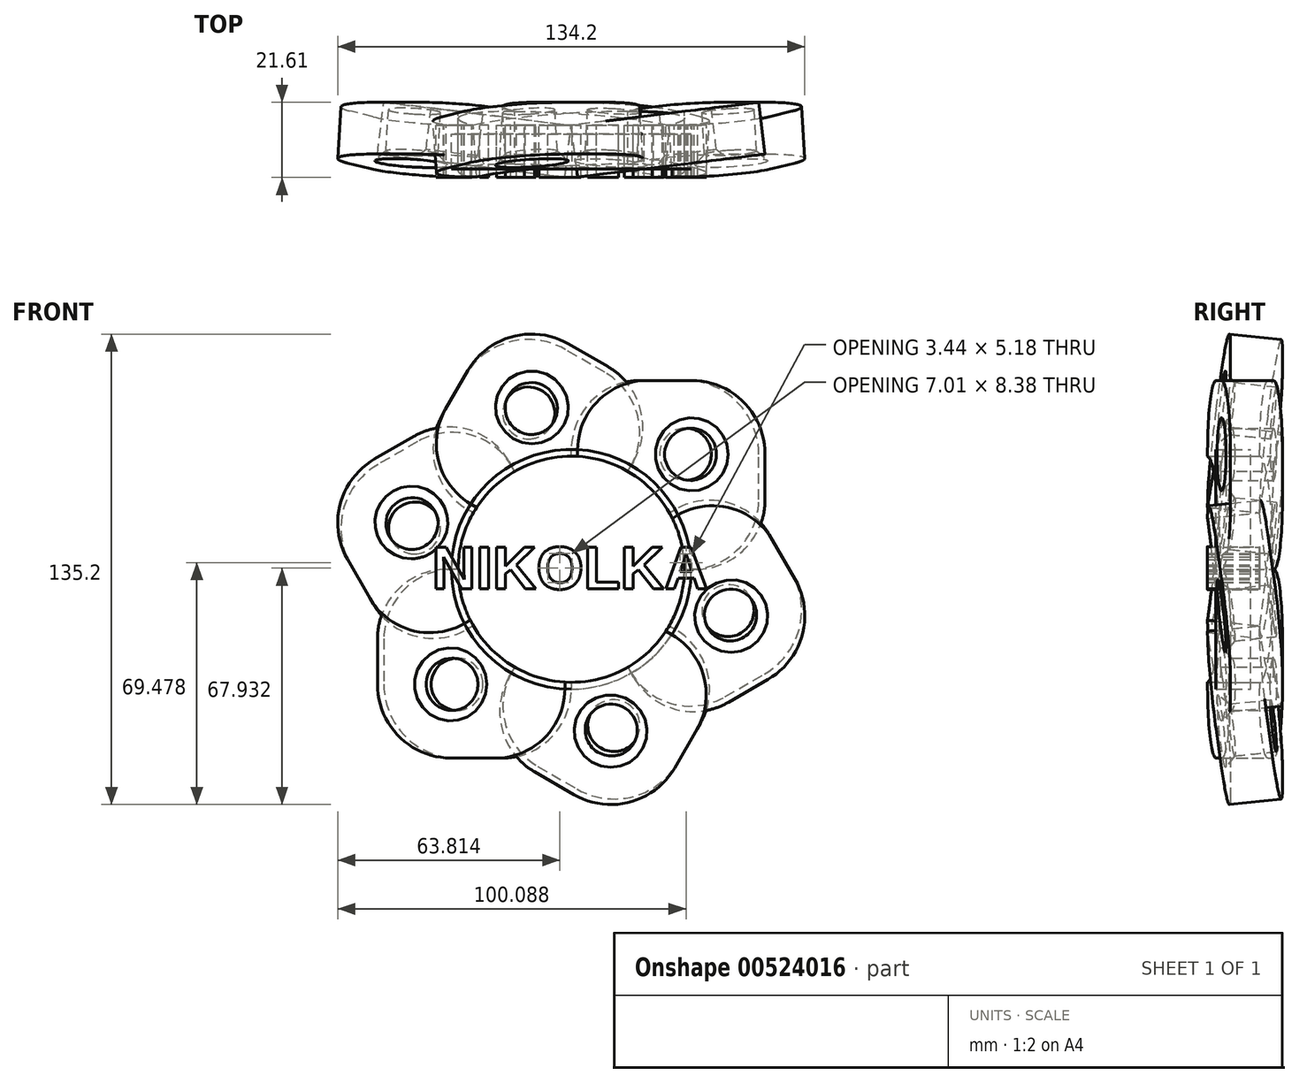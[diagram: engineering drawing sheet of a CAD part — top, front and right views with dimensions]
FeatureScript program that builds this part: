
annotation { "Feature Type Name" : "Feature", "Feature Type Description" : "" }
export const myFeature = defineFeature(function(context is Context, id is Id, definition is map)
    precondition{}
    {
        {
            var Q0;
            Q0=qCreatedBy(makeId("Front.planeOp"),FACE);
            var sketch = newSketch(context, id + "F0", { "sketchPlane" : qUnion([Q0])});
            skLineSegment(sketch, "E0.bottom", {"start": v(0, 0) * mm, "end": v(34.25, 0) * mm});
            skLineSegment(sketch, "E0.top", {"start": v(20, 54.25) * mm, "end": v(33.05, 54.25) * mm});
            skLineSegment(sketch, "E0.left", {"start": v(0, 0) * mm, "end": v(0, 34.25) * mm});
            skLineSegment(sketch, "E0.right", {"start": v(54.25, 20) * mm, "end": v(54.25, 33.05) * mm});
            skPoint(sketch, "E1.visualSharp", {"position": v(54.25, 54.25) * mm});
            skArc(sketch, "E1.filletArc", {"start": v(54.25, 33.05) * mm, "mid": v(48.04, 48.04) * mm, "end": v(33.05, 54.25) * mm});
            skPoint(sketch, "E2.visualSharp", {"position": v(0, 54.25) * mm});
            skArc(sketch, "E2.filletArc", {"start": v(20, 54.25) * mm, "mid": v(5.86, 48.4) * mm, "end": v(0, 34.25) * mm});
            skPoint(sketch, "E3.visualSharp", {"position": v(54.25, 0) * mm});
            skArc(sketch, "E3.filletArc", {"start": v(34.25, 0) * mm, "mid": v(48.4, 5.86) * mm, "end": v(54.25, 20) * mm});
            skCircle(sketch, "E4", {"center": v(33.05, 33.05) * mm, "radius": 7.5 * mm});
            skSolve(sketch);
        }
        {
            var Q0;
            Q0 = qSketchRegion(id + "F0", true);
            extrude(context, id + "F1", {"entities" : qUnion([Q0]), "endBound" : BoundingType.SYMMETRIC, "depth" : 15 * mm, "offsetDistance" : 25 * mm});
        }
        {
            var Q0;
            Q0=makeQuery(id+"F1.opExtrude","SWEPT_BODY",BODY,{"disambiguationData":[OSD([sQuery(id+"F0.wireOp",EDGE,"E0.bottom"),sQuery(id+"F0.wireOp",EDGE,"E0.top"),sQuery(id+"F0.wireOp",EDGE,"E0.left"),sQuery(id+"F0.wireOp",EDGE,"E0.right"),sQuery(id+"F0.wireOp",EDGE,"E1.filletArc"),sQuery(id+"F0.wireOp",EDGE,"E2.filletArc"),sQuery(id+"F0.wireOp",EDGE,"E3.filletArc")])]});
            var Q1;
            Q1=sQuery(id+"F0.wireOp",VERTEX,"E0.left.start");
            var Q2;
            Q2=makeQuery(id+"F1.opExtrude","SWEPT_EDGE",EDGE,{"disambiguationData":[OSD([sQuery(id+"F0.wireOp",EDGE,"E0.bottom"),sQuery(id+"F0.wireOp",EDGE,"E0.left")])]});
            transform(context, id + "F2", {"entities" : qUnion([Q0]), "transformType" : TransformType.ROTATION, "transformAxis" : qUnion([Q2]), "angle" : 60 * degree, "makeCopy" : true});
        }
        {
            var Q0;
            Q0=makeQuery(id+"F2.opPattern","COPY",BODY,{"derivedFrom":makeQuery(id+"F1.opExtrude","SWEPT_BODY",BODY,{"disambiguationData":[OSD([sQuery(id+"F0.wireOp",EDGE,"E0.bottom"),sQuery(id+"F0.wireOp",EDGE,"E0.top"),sQuery(id+"F0.wireOp",EDGE,"E0.left"),sQuery(id+"F0.wireOp",EDGE,"E0.right"),sQuery(id+"F0.wireOp",EDGE,"E1.filletArc"),sQuery(id+"F0.wireOp",EDGE,"E2.filletArc"),sQuery(id+"F0.wireOp",EDGE,"E3.filletArc")])]}),"instanceName":"1"});
            var Q1;
            Q1=makeQuery(id+"F1.opExtrude","SWEPT_EDGE",EDGE,{"disambiguationData":[OSD([sQuery(id+"F0.wireOp",EDGE,"E0.bottom"),sQuery(id+"F0.wireOp",EDGE,"E0.left")])]});
            transform(context, id + "F3", {"entities" : qUnion([Q0]), "transformType" : TransformType.ROTATION, "transformAxis" : qUnion([Q1]), "angle" : 60 * degree, "makeCopy" : true});
        }
        {
            var Q0;
            Q0=makeQuery(id+"F3.opPattern","COPY",BODY,{"derivedFrom":makeQuery(id+"F2.opPattern","COPY",BODY,{"derivedFrom":makeQuery(id+"F1.opExtrude","SWEPT_BODY",BODY,{"disambiguationData":[OSD([sQuery(id+"F0.wireOp",EDGE,"E0.bottom"),sQuery(id+"F0.wireOp",EDGE,"E0.top"),sQuery(id+"F0.wireOp",EDGE,"E0.left"),sQuery(id+"F0.wireOp",EDGE,"E0.right"),sQuery(id+"F0.wireOp",EDGE,"E1.filletArc"),sQuery(id+"F0.wireOp",EDGE,"E2.filletArc"),sQuery(id+"F0.wireOp",EDGE,"E3.filletArc")])]}),"instanceName":"1"}),"instanceName":"1"});
            var Q1;
            Q1=makeQuery(id+"F1.opExtrude","SWEPT_EDGE",EDGE,{"disambiguationData":[OSD([sQuery(id+"F0.wireOp",EDGE,"E0.bottom"),sQuery(id+"F0.wireOp",EDGE,"E0.left")])]});
            transform(context, id + "F4", {"entities" : qUnion([Q0]), "transformType" : TransformType.ROTATION, "transformAxis" : qUnion([Q1]), "angle" : 60 * degree, "makeCopy" : true});
        }
        {
            var Q0;
            Q0=makeQuery(id+"F4.opPattern","COPY",BODY,{"derivedFrom":makeQuery(id+"F3.opPattern","COPY",BODY,{"derivedFrom":makeQuery(id+"F2.opPattern","COPY",BODY,{"derivedFrom":makeQuery(id+"F1.opExtrude","SWEPT_BODY",BODY,{"disambiguationData":[OSD([sQuery(id+"F0.wireOp",EDGE,"E0.bottom"),sQuery(id+"F0.wireOp",EDGE,"E0.top"),sQuery(id+"F0.wireOp",EDGE,"E0.left"),sQuery(id+"F0.wireOp",EDGE,"E0.right"),sQuery(id+"F0.wireOp",EDGE,"E1.filletArc"),sQuery(id+"F0.wireOp",EDGE,"E2.filletArc"),sQuery(id+"F0.wireOp",EDGE,"E3.filletArc")])]}),"instanceName":"1"}),"instanceName":"1"}),"instanceName":"1"});
            var Q1;
            Q1=makeQuery(id+"F1.opExtrude","SWEPT_EDGE",EDGE,{"disambiguationData":[OSD([sQuery(id+"F0.wireOp",EDGE,"E0.bottom"),sQuery(id+"F0.wireOp",EDGE,"E0.left")])]});
            transform(context, id + "F5", {"entities" : qUnion([Q0]), "transformType" : TransformType.ROTATION, "transformAxis" : qUnion([Q1]), "angle" : 60 * degree, "makeCopy" : false});
        }
        {
            var Q0;
            Q0=makeQuery(id+"F4.opPattern","COPY",BODY,{"derivedFrom":makeQuery(id+"F3.opPattern","COPY",BODY,{"derivedFrom":makeQuery(id+"F2.opPattern","COPY",BODY,{"derivedFrom":makeQuery(id+"F1.opExtrude","SWEPT_BODY",BODY,{"disambiguationData":[OSD([sQuery(id+"F0.wireOp",EDGE,"E0.bottom"),sQuery(id+"F0.wireOp",EDGE,"E0.top"),sQuery(id+"F0.wireOp",EDGE,"E0.left"),sQuery(id+"F0.wireOp",EDGE,"E0.right"),sQuery(id+"F0.wireOp",EDGE,"E1.filletArc"),sQuery(id+"F0.wireOp",EDGE,"E2.filletArc"),sQuery(id+"F0.wireOp",EDGE,"E3.filletArc")])]}),"instanceName":"1"}),"instanceName":"1"}),"instanceName":"1"});
            var Q1;
            Q1=makeQuery(id+"F1.opExtrude","SWEPT_EDGE",EDGE,{"disambiguationData":[OSD([sQuery(id+"F0.wireOp",EDGE,"E0.bottom"),sQuery(id+"F0.wireOp",EDGE,"E0.left")])]});
            transform(context, id + "F6", {"entities" : qUnion([Q0]), "transformType" : TransformType.ROTATION, "transformAxis" : qUnion([Q1]), "angle" : 60 * degree, "makeCopy" : true});
        }
        {
            var Q0;
            Q0=makeQuery(id+"F3.opPattern","COPY",BODY,{"derivedFrom":makeQuery(id+"F2.opPattern","COPY",BODY,{"derivedFrom":makeQuery(id+"F1.opExtrude","SWEPT_BODY",BODY,{"disambiguationData":[OSD([sQuery(id+"F0.wireOp",EDGE,"E0.bottom"),sQuery(id+"F0.wireOp",EDGE,"E0.top"),sQuery(id+"F0.wireOp",EDGE,"E0.left"),sQuery(id+"F0.wireOp",EDGE,"E0.right"),sQuery(id+"F0.wireOp",EDGE,"E1.filletArc"),sQuery(id+"F0.wireOp",EDGE,"E2.filletArc"),sQuery(id+"F0.wireOp",EDGE,"E3.filletArc")])]}),"instanceName":"1"}),"instanceName":"1"});
            var Q1;
            Q1=makeQuery(id+"F1.opExtrude","SWEPT_EDGE",EDGE,{"disambiguationData":[OSD([sQuery(id+"F0.wireOp",EDGE,"E0.bottom"),sQuery(id+"F0.wireOp",EDGE,"E0.left")])]});
            transform(context, id + "F7", {"entities" : qUnion([Q0]), "transformType" : TransformType.ROTATION, "transformAxis" : qUnion([Q1]), "angle" : 60 * degree, "makeCopy" : true});
        }
        {
            var Q0;
            Q0=makeQuery(id+"F1.opExtrude","SWEPT_BODY",BODY,{"disambiguationData":[OSD([sQuery(id+"F0.wireOp",EDGE,"E0.bottom"),sQuery(id+"F0.wireOp",EDGE,"E0.top"),sQuery(id+"F0.wireOp",EDGE,"E0.left"),sQuery(id+"F0.wireOp",EDGE,"E0.right"),sQuery(id+"F0.wireOp",EDGE,"E1.filletArc"),sQuery(id+"F0.wireOp",EDGE,"E2.filletArc"),sQuery(id+"F0.wireOp",EDGE,"E3.filletArc")])]});
            var Q1;
            Q1=makeQuery(id+"F1.opExtrude","CAP_EDGE",EDGE,{"disambiguationData":[OSD([sQuery(id+"F0.wireOp",EDGE,"E0.left")])],"isStart":true});
            transform(context, id + "F8", {"entities" : qUnion([Q0]), "transformType" : TransformType.ROTATION, "transformAxis" : qUnion([Q1]), "angle" : 7 * degree, "makeCopy" : false});
        }
        {
            var Q0;
            Q0=makeQuery(id+"F6.opPattern","COPY",BODY,{"derivedFrom":makeQuery(id+"F4.opPattern","COPY",BODY,{"derivedFrom":makeQuery(id+"F3.opPattern","COPY",BODY,{"derivedFrom":makeQuery(id+"F2.opPattern","COPY",BODY,{"derivedFrom":makeQuery(id+"F1.opExtrude","SWEPT_BODY",BODY,{"disambiguationData":[OSD([sQuery(id+"F0.wireOp",EDGE,"E0.bottom"),sQuery(id+"F0.wireOp",EDGE,"E0.top"),sQuery(id+"F0.wireOp",EDGE,"E0.left"),sQuery(id+"F0.wireOp",EDGE,"E0.right"),sQuery(id+"F0.wireOp",EDGE,"E1.filletArc"),sQuery(id+"F0.wireOp",EDGE,"E2.filletArc"),sQuery(id+"F0.wireOp",EDGE,"E3.filletArc")])]}),"instanceName":"1"}),"instanceName":"1"}),"instanceName":"1"}),"instanceName":"1"});
            var Q1;
            Q1=makeQuery(id+"F6.opPattern","COPY",EDGE,{"derivedFrom":makeQuery(id+"F4.opPattern","COPY",EDGE,{"derivedFrom":makeQuery(id+"F3.opPattern","COPY",EDGE,{"derivedFrom":makeQuery(id+"F2.opPattern","COPY",EDGE,{"derivedFrom":makeQuery(id+"F1.opExtrude","CAP_EDGE",EDGE,{"disambiguationData":[OSD([sQuery(id+"F0.wireOp",EDGE,"E0.left")])],"isStart":true}),"instanceName":"1"}),"instanceName":"1"}),"instanceName":"1"}),"instanceName":"1"});
            transform(context, id + "F9", {"entities" : qUnion([Q0]), "transformType" : TransformType.ROTATION, "transformAxis" : qUnion([Q1]), "angle" : 7 * degree, "makeCopy" : false});
        }
        {
            var Q0;
            Q0=makeQuery(id+"F4.opPattern","COPY",BODY,{"derivedFrom":makeQuery(id+"F3.opPattern","COPY",BODY,{"derivedFrom":makeQuery(id+"F2.opPattern","COPY",BODY,{"derivedFrom":makeQuery(id+"F1.opExtrude","SWEPT_BODY",BODY,{"disambiguationData":[OSD([sQuery(id+"F0.wireOp",EDGE,"E0.bottom"),sQuery(id+"F0.wireOp",EDGE,"E0.top"),sQuery(id+"F0.wireOp",EDGE,"E0.left"),sQuery(id+"F0.wireOp",EDGE,"E0.right"),sQuery(id+"F0.wireOp",EDGE,"E1.filletArc"),sQuery(id+"F0.wireOp",EDGE,"E2.filletArc"),sQuery(id+"F0.wireOp",EDGE,"E3.filletArc")])]}),"instanceName":"1"}),"instanceName":"1"}),"instanceName":"1"});
            var Q1;
            Q1=makeQuery(id+"F4.opPattern","COPY",EDGE,{"derivedFrom":makeQuery(id+"F3.opPattern","COPY",EDGE,{"derivedFrom":makeQuery(id+"F2.opPattern","COPY",EDGE,{"derivedFrom":makeQuery(id+"F1.opExtrude","CAP_EDGE",EDGE,{"disambiguationData":[OSD([sQuery(id+"F0.wireOp",EDGE,"E0.left")])],"isStart":true}),"instanceName":"1"}),"instanceName":"1"}),"instanceName":"1"});
            transform(context, id + "F10", {"entities" : qUnion([Q0]), "transformType" : TransformType.ROTATION, "transformAxis" : qUnion([Q1]), "angle" : 7 * degree, "makeCopy" : false});
        }
        {
            var Q0;
            Q0=makeQuery(id+"F7.opPattern","COPY",BODY,{"derivedFrom":makeQuery(id+"F3.opPattern","COPY",BODY,{"derivedFrom":makeQuery(id+"F2.opPattern","COPY",BODY,{"derivedFrom":makeQuery(id+"F1.opExtrude","SWEPT_BODY",BODY,{"disambiguationData":[OSD([sQuery(id+"F0.wireOp",EDGE,"E0.bottom"),sQuery(id+"F0.wireOp",EDGE,"E0.top"),sQuery(id+"F0.wireOp",EDGE,"E0.left"),sQuery(id+"F0.wireOp",EDGE,"E0.right"),sQuery(id+"F0.wireOp",EDGE,"E1.filletArc"),sQuery(id+"F0.wireOp",EDGE,"E2.filletArc"),sQuery(id+"F0.wireOp",EDGE,"E3.filletArc")])]}),"instanceName":"1"}),"instanceName":"1"}),"instanceName":"1"});
            var Q1;
            Q1=makeQuery(id+"F7.opPattern","COPY",EDGE,{"derivedFrom":makeQuery(id+"F3.opPattern","COPY",EDGE,{"derivedFrom":makeQuery(id+"F2.opPattern","COPY",EDGE,{"derivedFrom":makeQuery(id+"F1.opExtrude","CAP_EDGE",EDGE,{"disambiguationData":[OSD([sQuery(id+"F0.wireOp",EDGE,"E0.left")])],"isStart":true}),"instanceName":"1"}),"instanceName":"1"}),"instanceName":"1"});
            transform(context, id + "F11", {"entities" : qUnion([Q0]), "transformType" : TransformType.ROTATION, "transformAxis" : qUnion([Q1]), "angle" : 7 * degree, "makeCopy" : false});
        }
        {
            var Q0;
            Q0=makeQuery(id+"F3.opPattern","COPY",BODY,{"derivedFrom":makeQuery(id+"F2.opPattern","COPY",BODY,{"derivedFrom":makeQuery(id+"F1.opExtrude","SWEPT_BODY",BODY,{"disambiguationData":[OSD([sQuery(id+"F0.wireOp",EDGE,"E0.bottom"),sQuery(id+"F0.wireOp",EDGE,"E0.top"),sQuery(id+"F0.wireOp",EDGE,"E0.left"),sQuery(id+"F0.wireOp",EDGE,"E0.right"),sQuery(id+"F0.wireOp",EDGE,"E1.filletArc"),sQuery(id+"F0.wireOp",EDGE,"E2.filletArc"),sQuery(id+"F0.wireOp",EDGE,"E3.filletArc")])]}),"instanceName":"1"}),"instanceName":"1"});
            var Q1;
            Q1=makeQuery(id+"F3.opPattern","COPY",EDGE,{"derivedFrom":makeQuery(id+"F2.opPattern","COPY",EDGE,{"derivedFrom":makeQuery(id+"F1.opExtrude","CAP_EDGE",EDGE,{"disambiguationData":[OSD([sQuery(id+"F0.wireOp",EDGE,"E0.left")])],"isStart":true}),"instanceName":"1"}),"instanceName":"1"});
            transform(context, id + "F12", {"entities" : qUnion([Q0]), "transformType" : TransformType.ROTATION, "transformAxis" : qUnion([Q1]), "angle" : 7 * degree, "makeCopy" : false});
        }
        {
            var Q0;
            Q0=makeQuery(id+"F2.opPattern","COPY",BODY,{"derivedFrom":makeQuery(id+"F1.opExtrude","SWEPT_BODY",BODY,{"disambiguationData":[OSD([sQuery(id+"F0.wireOp",EDGE,"E0.bottom"),sQuery(id+"F0.wireOp",EDGE,"E0.top"),sQuery(id+"F0.wireOp",EDGE,"E0.left"),sQuery(id+"F0.wireOp",EDGE,"E0.right"),sQuery(id+"F0.wireOp",EDGE,"E1.filletArc"),sQuery(id+"F0.wireOp",EDGE,"E2.filletArc"),sQuery(id+"F0.wireOp",EDGE,"E3.filletArc")])]}),"instanceName":"1"});
            var Q1;
            Q1=makeQuery(id+"F2.opPattern","COPY",EDGE,{"derivedFrom":makeQuery(id+"F1.opExtrude","CAP_EDGE",EDGE,{"disambiguationData":[OSD([sQuery(id+"F0.wireOp",EDGE,"E0.left")])],"isStart":true}),"instanceName":"1"});
            transform(context, id + "F13", {"entities" : qUnion([Q0]), "transformType" : TransformType.ROTATION, "transformAxis" : qUnion([Q1]), "angle" : 7 * degree, "makeCopy" : false});
        }
        {
            var Q0;
            Q0=makeQuery(id+"F1.opExtrude","CAP_EDGE",EDGE,{"disambiguationData":[OSD([sQuery(id+"F0.wireOp",EDGE,"E4")])],"isStart":false});
            var Q1;
            Q1=makeQuery(id+"F2.opPattern","COPY",EDGE,{"derivedFrom":makeQuery(id+"F1.opExtrude","CAP_EDGE",EDGE,{"disambiguationData":[OSD([sQuery(id+"F0.wireOp",EDGE,"E4")])],"isStart":false}),"instanceName":"1"});
            var Q2;
            Q2=makeQuery(id+"F3.opPattern","COPY",EDGE,{"derivedFrom":makeQuery(id+"F2.opPattern","COPY",EDGE,{"derivedFrom":makeQuery(id+"F1.opExtrude","CAP_EDGE",EDGE,{"disambiguationData":[OSD([sQuery(id+"F0.wireOp",EDGE,"E4")])],"isStart":false}),"instanceName":"1"}),"instanceName":"1"});
            var Q3;
            Q3=makeQuery(id+"F7.opPattern","COPY",EDGE,{"derivedFrom":makeQuery(id+"F3.opPattern","COPY",EDGE,{"derivedFrom":makeQuery(id+"F2.opPattern","COPY",EDGE,{"derivedFrom":makeQuery(id+"F1.opExtrude","CAP_EDGE",EDGE,{"disambiguationData":[OSD([sQuery(id+"F0.wireOp",EDGE,"E4")])],"isStart":false}),"instanceName":"1"}),"instanceName":"1"}),"instanceName":"1"});
            var Q4;
            Q4=makeQuery(id+"F4.opPattern","COPY",EDGE,{"derivedFrom":makeQuery(id+"F3.opPattern","COPY",EDGE,{"derivedFrom":makeQuery(id+"F2.opPattern","COPY",EDGE,{"derivedFrom":makeQuery(id+"F1.opExtrude","CAP_EDGE",EDGE,{"disambiguationData":[OSD([sQuery(id+"F0.wireOp",EDGE,"E4")])],"isStart":false}),"instanceName":"1"}),"instanceName":"1"}),"instanceName":"1"});
            var Q5;
            Q5=makeQuery(id+"F6.opPattern","COPY",EDGE,{"derivedFrom":makeQuery(id+"F4.opPattern","COPY",EDGE,{"derivedFrom":makeQuery(id+"F3.opPattern","COPY",EDGE,{"derivedFrom":makeQuery(id+"F2.opPattern","COPY",EDGE,{"derivedFrom":makeQuery(id+"F1.opExtrude","CAP_EDGE",EDGE,{"disambiguationData":[OSD([sQuery(id+"F0.wireOp",EDGE,"E4")])],"isStart":false}),"instanceName":"1"}),"instanceName":"1"}),"instanceName":"1"}),"instanceName":"1"});
            chamfer(context, id + "F14", {"entities" : qUnion([Q0, Q1, Q2, Q3, Q4, Q5]), "width" : 3 * mm, "tangentPropagation" : true});
        }
        {
            var Q0;
            Q0=qCreatedBy(makeId("Front.planeOp"),FACE);
            var sketch = newSketch(context, id + "F15", { "sketchPlane" : qUnion([Q0])});
            skCircle(sketch, "E5", {"center": v(0, 0) * mm, "radius": 32.5 * mm});
            skSolve(sketch);
        }
        {
            var Q0;
            Q0 = qSketchRegion(id + "F15", true);
            extrude(context, id + "F16", {"entities" : qUnion([Q0]), "endBound" : BoundingType.SYMMETRIC, "depth" : 35 * mm, "offsetDistance" : 25 * mm});
        }
        {
            var Q0;
            Q0=makeQuery(id+"F16.opExtrude","SWEPT_BODY",BODY,{"disambiguationData":[OSD([sQuery(id+"F15.wireOp",EDGE,"E5")])]});
            var Q1;
            Q1=makeQuery(id+"F6.opPattern","COPY",BODY,{"derivedFrom":makeQuery(id+"F4.opPattern","COPY",BODY,{"derivedFrom":makeQuery(id+"F3.opPattern","COPY",BODY,{"derivedFrom":makeQuery(id+"F2.opPattern","COPY",BODY,{"derivedFrom":makeQuery(id+"F1.opExtrude","SWEPT_BODY",BODY,{"disambiguationData":[OSD([sQuery(id+"F0.wireOp",EDGE,"E0.bottom"),sQuery(id+"F0.wireOp",EDGE,"E0.top"),sQuery(id+"F0.wireOp",EDGE,"E0.left"),sQuery(id+"F0.wireOp",EDGE,"E0.right"),sQuery(id+"F0.wireOp",EDGE,"E1.filletArc"),sQuery(id+"F0.wireOp",EDGE,"E2.filletArc"),sQuery(id+"F0.wireOp",EDGE,"E3.filletArc"),sQuery(id+"F0.wireOp",EDGE,"E4")])]}),"instanceName":"1"}),"instanceName":"1"}),"instanceName":"1"}),"instanceName":"1"});
            var Q2;
            Q2=makeQuery(id+"F4.opPattern","COPY",BODY,{"derivedFrom":makeQuery(id+"F3.opPattern","COPY",BODY,{"derivedFrom":makeQuery(id+"F2.opPattern","COPY",BODY,{"derivedFrom":makeQuery(id+"F1.opExtrude","SWEPT_BODY",BODY,{"disambiguationData":[OSD([sQuery(id+"F0.wireOp",EDGE,"E0.bottom"),sQuery(id+"F0.wireOp",EDGE,"E0.top"),sQuery(id+"F0.wireOp",EDGE,"E0.left"),sQuery(id+"F0.wireOp",EDGE,"E0.right"),sQuery(id+"F0.wireOp",EDGE,"E1.filletArc"),sQuery(id+"F0.wireOp",EDGE,"E2.filletArc"),sQuery(id+"F0.wireOp",EDGE,"E3.filletArc"),sQuery(id+"F0.wireOp",EDGE,"E4")])]}),"instanceName":"1"}),"instanceName":"1"}),"instanceName":"1"});
            var Q3;
            Q3=makeQuery(id+"F7.opPattern","COPY",BODY,{"derivedFrom":makeQuery(id+"F3.opPattern","COPY",BODY,{"derivedFrom":makeQuery(id+"F2.opPattern","COPY",BODY,{"derivedFrom":makeQuery(id+"F1.opExtrude","SWEPT_BODY",BODY,{"disambiguationData":[OSD([sQuery(id+"F0.wireOp",EDGE,"E0.bottom"),sQuery(id+"F0.wireOp",EDGE,"E0.top"),sQuery(id+"F0.wireOp",EDGE,"E0.left"),sQuery(id+"F0.wireOp",EDGE,"E0.right"),sQuery(id+"F0.wireOp",EDGE,"E1.filletArc"),sQuery(id+"F0.wireOp",EDGE,"E2.filletArc"),sQuery(id+"F0.wireOp",EDGE,"E3.filletArc"),sQuery(id+"F0.wireOp",EDGE,"E4")])]}),"instanceName":"1"}),"instanceName":"1"}),"instanceName":"1"});
            var Q4;
            Q4=makeQuery(id+"F3.opPattern","COPY",BODY,{"derivedFrom":makeQuery(id+"F2.opPattern","COPY",BODY,{"derivedFrom":makeQuery(id+"F1.opExtrude","SWEPT_BODY",BODY,{"disambiguationData":[OSD([sQuery(id+"F0.wireOp",EDGE,"E0.bottom"),sQuery(id+"F0.wireOp",EDGE,"E0.top"),sQuery(id+"F0.wireOp",EDGE,"E0.left"),sQuery(id+"F0.wireOp",EDGE,"E0.right"),sQuery(id+"F0.wireOp",EDGE,"E1.filletArc"),sQuery(id+"F0.wireOp",EDGE,"E2.filletArc"),sQuery(id+"F0.wireOp",EDGE,"E3.filletArc"),sQuery(id+"F0.wireOp",EDGE,"E4")])]}),"instanceName":"1"}),"instanceName":"1"});
            var Q5;
            Q5=makeQuery(id+"F2.opPattern","COPY",BODY,{"derivedFrom":makeQuery(id+"F1.opExtrude","SWEPT_BODY",BODY,{"disambiguationData":[OSD([sQuery(id+"F0.wireOp",EDGE,"E0.bottom"),sQuery(id+"F0.wireOp",EDGE,"E0.top"),sQuery(id+"F0.wireOp",EDGE,"E0.left"),sQuery(id+"F0.wireOp",EDGE,"E0.right"),sQuery(id+"F0.wireOp",EDGE,"E1.filletArc"),sQuery(id+"F0.wireOp",EDGE,"E2.filletArc"),sQuery(id+"F0.wireOp",EDGE,"E3.filletArc"),sQuery(id+"F0.wireOp",EDGE,"E4")])]}),"instanceName":"1"});
            var Q6;
            Q6=makeQuery(id+"F1.opExtrude","SWEPT_BODY",BODY,{"disambiguationData":[OSD([sQuery(id+"F0.wireOp",EDGE,"E0.bottom"),sQuery(id+"F0.wireOp",EDGE,"E0.top"),sQuery(id+"F0.wireOp",EDGE,"E0.left"),sQuery(id+"F0.wireOp",EDGE,"E0.right"),sQuery(id+"F0.wireOp",EDGE,"E1.filletArc"),sQuery(id+"F0.wireOp",EDGE,"E2.filletArc"),sQuery(id+"F0.wireOp",EDGE,"E3.filletArc"),sQuery(id+"F0.wireOp",EDGE,"E4")])]});
            booleanBodies(context, id + "F17", {"operationType" : BooleanOperationType.SUBTRACTION, "tools" : qUnion([Q0]), "targets" : qUnion([Q1, Q2, Q3, Q4, Q5, Q6])});
        }
        {
            var Q0;
            Q0=qCreatedBy(makeId("Front.planeOp"),FACE);
            var sketch = newSketch(context, id + "F18", { "sketchPlane" : qUnion([Q0])});
            skCircle(sketch, "E6", {"center": v(0, 0) * mm, "radius": 34.45 * mm});
            skSolve(sketch);
        }
        {
            var Q0;
            Q0 = qSketchRegion(id + "F18", true);
            extrude(context, id + "F19", {"entities" : qUnion([Q0]), "endBound" : BoundingType.SYMMETRIC, "depth" : 10 * mm, "offsetDistance" : 25 * mm});
        }
        {
            var Q0;
            Q0=qCreatedBy(makeId("Front.planeOp"),FACE);
            var sketch = newSketch(context, id + "F20", { "sketchPlane" : qUnion([Q0])});
            skText(sketch, "E7", { "text": "NIKOLKA", "fontName": "Arimo-Bold.ttf"});
            const initialGuessF20  = {"E7": [-0.04, -0.00566, 1, 0, 0.01253]};
            skSetInitialGuess(sketch, initialGuessF20);
            skSolve(sketch);
        }
        {
            var Q0;
            Q0 = qSketchRegion(id + "F20", true);
            extrude(context, id + "F21", {"entities" : qUnion([Q0]), "endBound" : BoundingType.SYMMETRIC, "depth" : 15 * mm, "offsetDistance" : 25 * mm});
        }
    });
